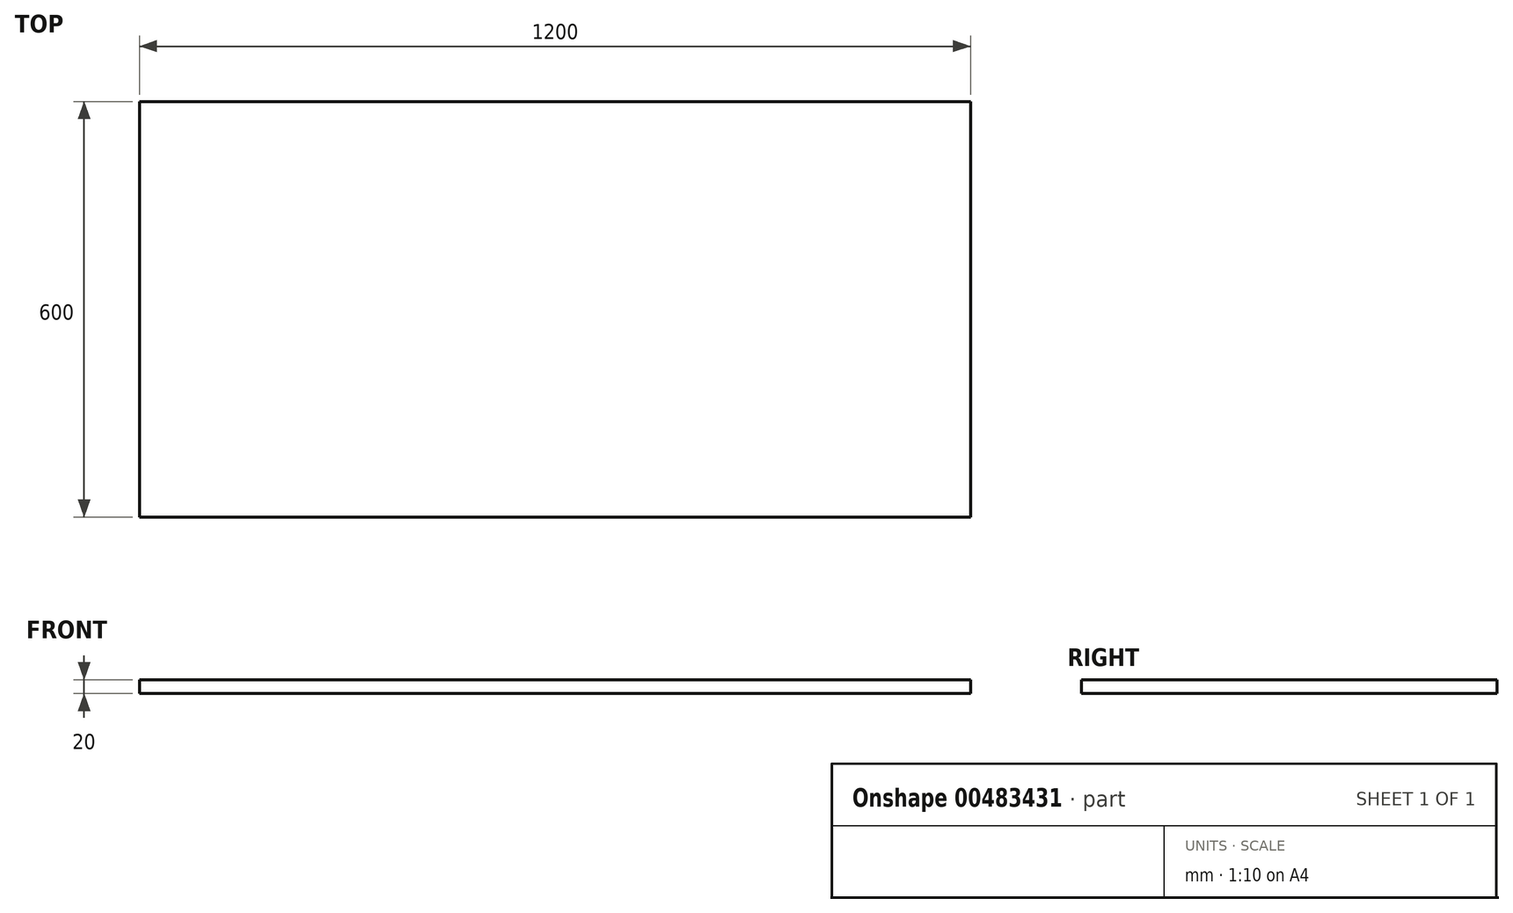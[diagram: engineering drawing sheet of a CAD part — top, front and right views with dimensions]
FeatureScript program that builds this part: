
annotation { "Feature Type Name" : "Feature", "Feature Type Description" : "" }
export const myFeature = defineFeature(function(context is Context, id is Id, definition is map)
    precondition{}
    {
        {
            var Q0;
            Q0=qCreatedBy(makeId("Top.planeOp"),FACE);
            var sketch = newSketch(context, id + "F0", { "sketchPlane" : qUnion([Q0])});
            skLineSegment(sketch, "E0.bottom", {"start": v(616.07, -300) * mm, "end": v(-583.93, -300) * mm});
            skLineSegment(sketch, "E0.top", {"start": v(616.07, 300) * mm, "end": v(-583.93, 300) * mm});
            skLineSegment(sketch, "E0.left", {"start": v(616.07, -300) * mm, "end": v(616.07, 300) * mm});
            skLineSegment(sketch, "E0.right", {"start": v(-583.93, -300) * mm, "end": v(-583.93, 300) * mm});
            skPoint(sketch, "E0.middle", {"position": v(16.07, 0) * mm});
            skSolve(sketch);
        }
        {
            var Q0;
            Q0 = qSketchRegion(id + "F0", true);
            extrude(context, id + "F1", {"entities" : qUnion([Q0]), "depth" : 20 * mm, "offsetDistance" : 25 * mm});
        }
    });
